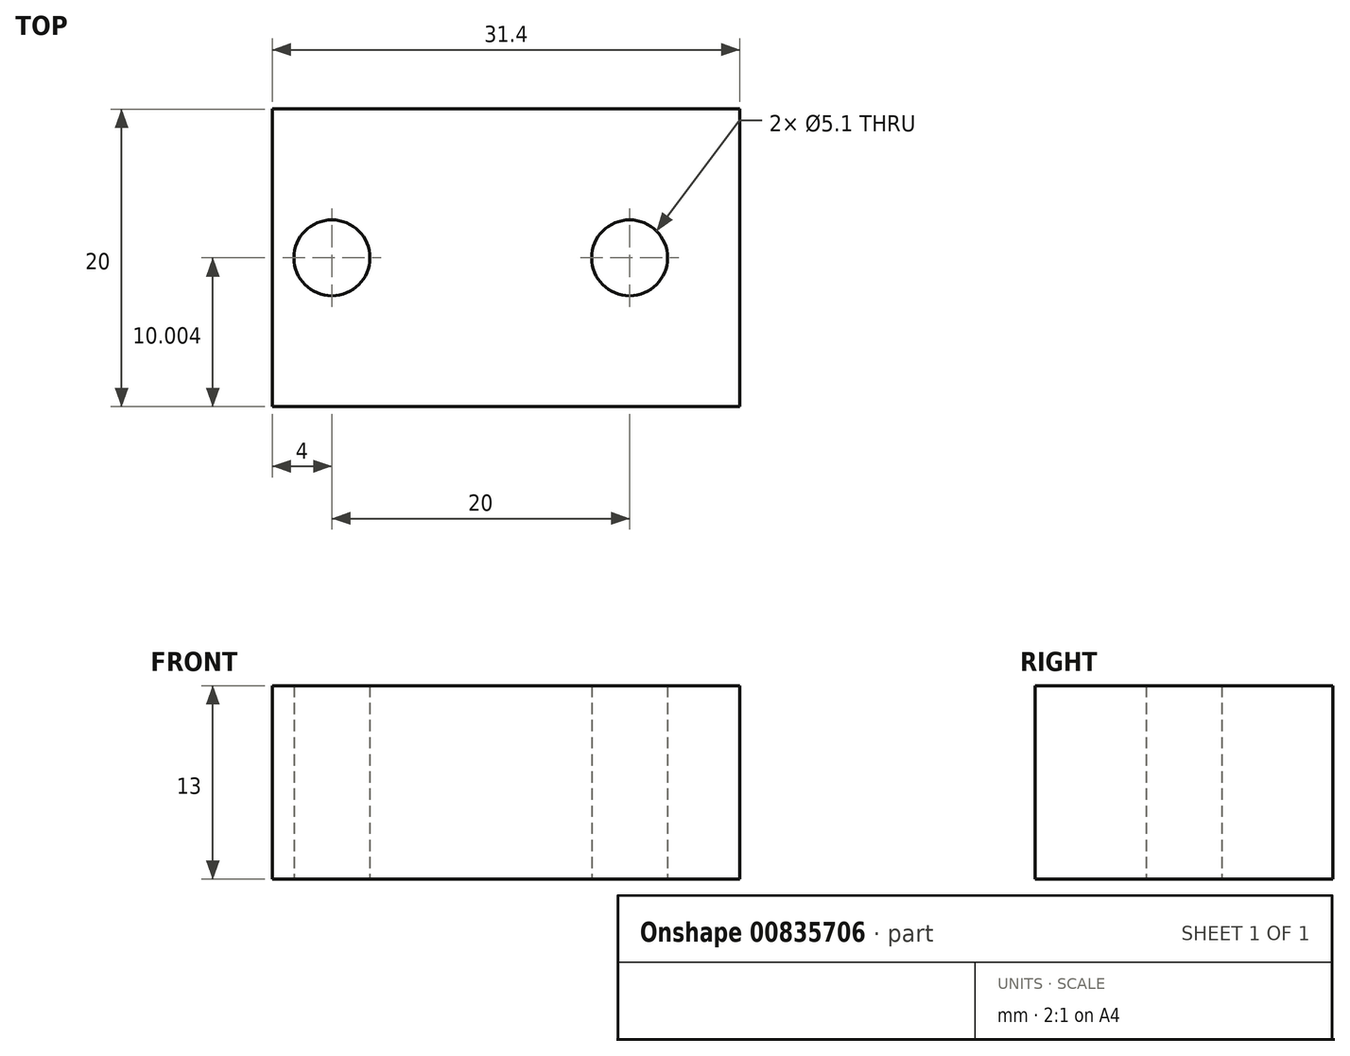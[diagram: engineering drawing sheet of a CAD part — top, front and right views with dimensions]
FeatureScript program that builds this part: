
annotation { "Feature Type Name" : "Feature", "Feature Type Description" : "" }
export const myFeature = defineFeature(function(context is Context, id is Id, definition is map)
    precondition{}
    {
        {
            var Q0;
            Q0=qCreatedBy(makeId("Top.planeOp"),FACE);
            var sketch = newSketch(context, id + "F0", { "sketchPlane" : qUnion([Q0])});
            skCircle(sketch, "E0", {"center": v(-55.34, -19.27) * mm, "radius": 2.05 * mm});
            skCircle(sketch, "E1", {"center": v(-55.34, -66.87) * mm, "radius": 2.05 * mm});
            skCircle(sketch, "E2", {"center": v(-46.19, -43.07) * mm, "radius": 2.55 * mm});
            skCircle(sketch, "E3", {"center": v(-26.19, -43.07) * mm, "radius": 2.55 * mm});
            skCircle(sketch, "E4", {"center": v(-97.34, -33.07) * mm, "radius": 1.59 * mm});
            skCircle(sketch, "E5", {"center": v(-77.34, -33.07) * mm, "radius": 1.59 * mm});
            skCircle(sketch, "E6", {"center": v(-97.34, -53.07) * mm, "radius": 1.59 * mm});
            skCircle(sketch, "E7", {"center": v(-77.34, -53.07) * mm, "radius": 1.59 * mm});
            skLineSegment(sketch, "E8.right", {"start": v(-18.79, -19.07) * mm, "end": v(-18.79, -67.07) * mm});
            skLineSegment(sketch, "E9", {"start": v(-102.38, -19.08) * mm, "end": v(-102.22, -67.08) * mm});
            skLineSegment(sketch, "E10", {"start": v(-97.38, -14.07) * mm, "end": v(-23.79, -14.07) * mm});
            skLineSegment(sketch, "E11", {"start": v(-23.79, -72.07) * mm, "end": v(-97.22, -72.07) * mm});
            skArc(sketch, "E12.filletArc", {"start": v(-97.38, -14.07) * mm, "mid": v(-100.93, -15.54) * mm, "end": v(-102.38, -19.08) * mm});
            skArc(sketch, "E13.filletArc", {"start": v(-18.79, -19.07) * mm, "mid": v(-20.25, -15.53) * mm, "end": v(-23.79, -14.07) * mm});
            skArc(sketch, "E14.filletArc", {"start": v(-23.79, -72.07) * mm, "mid": v(-20.25, -70.6) * mm, "end": v(-18.79, -67.07) * mm});
            skArc(sketch, "E15.filletArc", {"start": v(-102.22, -67.08) * mm, "mid": v(-100.75, -70.6) * mm, "end": v(-97.22, -72.07) * mm});
            skLineSegment(sketch, "E16.bottom", {"start": v(-18.79, -33.07) * mm, "end": v(-50.19, -33.07) * mm});
            skLineSegment(sketch, "E16.top", {"start": v(-18.79, -53.07) * mm, "end": v(-50.19, -53.07) * mm});
            skLineSegment(sketch, "E16.left", {"start": v(-18.79, -33.07) * mm, "end": v(-18.79, -53.07) * mm});
            skLineSegment(sketch, "E16.right", {"start": v(-50.19, -33.07) * mm, "end": v(-50.19, -53.07) * mm});
            skSolve(sketch);
        }
        {
            var Q0;
            Q0=makeQuery(id+"F0.imprint","IMPRINT",FACE,{"disambiguationData":[TD([[makeQuery(id+"F0.imprint","IMPRINT",EDGE,{"derivedFrom":sQuery(id+"F0.wireOp",EDGE,"E2")}),-1.0]])]});
            extrude(context, id + "F1", {"entities" : qUnion([Q0]), "depth" : 13 * mm, "offsetDistance" : 25 * mm});
        }
    });
